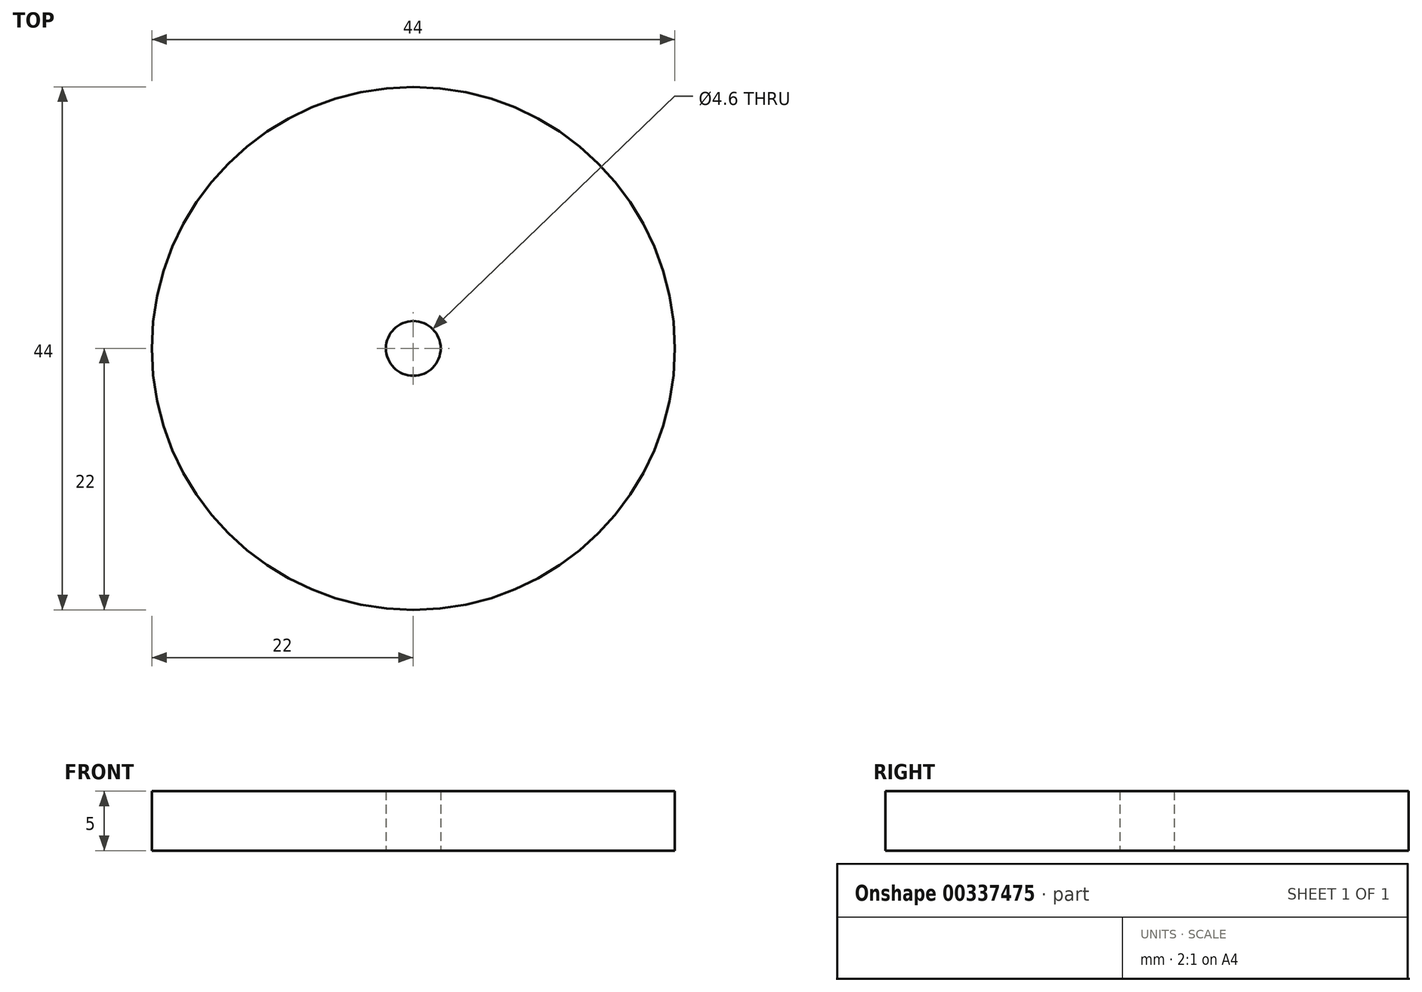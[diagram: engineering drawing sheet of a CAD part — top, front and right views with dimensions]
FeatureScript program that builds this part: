
annotation { "Feature Type Name" : "Feature", "Feature Type Description" : "" }
export const myFeature = defineFeature(function(context is Context, id is Id, definition is map)
    precondition{}
    {
        {
            var Q0;
            Q0=qCreatedBy(makeId("Top.planeOp"),FACE);
            var sketch = newSketch(context, id + "F0", { "sketchPlane" : qUnion([Q0])});
            skCircle(sketch, "E0", {"center": v(0, 0) * mm, "radius": 22 * mm});
            skCircle(sketch, "E1", {"center": v(0, 0) * mm, "radius": 2.3 * mm});
            skSolve(sketch);
        }
        {
            var Q0;
            Q0=makeQuery(id+"F0.imprint","IMPRINT",FACE,{"disambiguationData":[TD([[makeQuery(id+"F0.imprint","IMPRINT",EDGE,{"derivedFrom":sQuery(id+"F0.wireOp",EDGE,"E0")}),1.0]])]});
            extrude(context, id + "F1", {"entities" : qUnion([Q0]), "depth" : 5 * mm});
        }
    });
